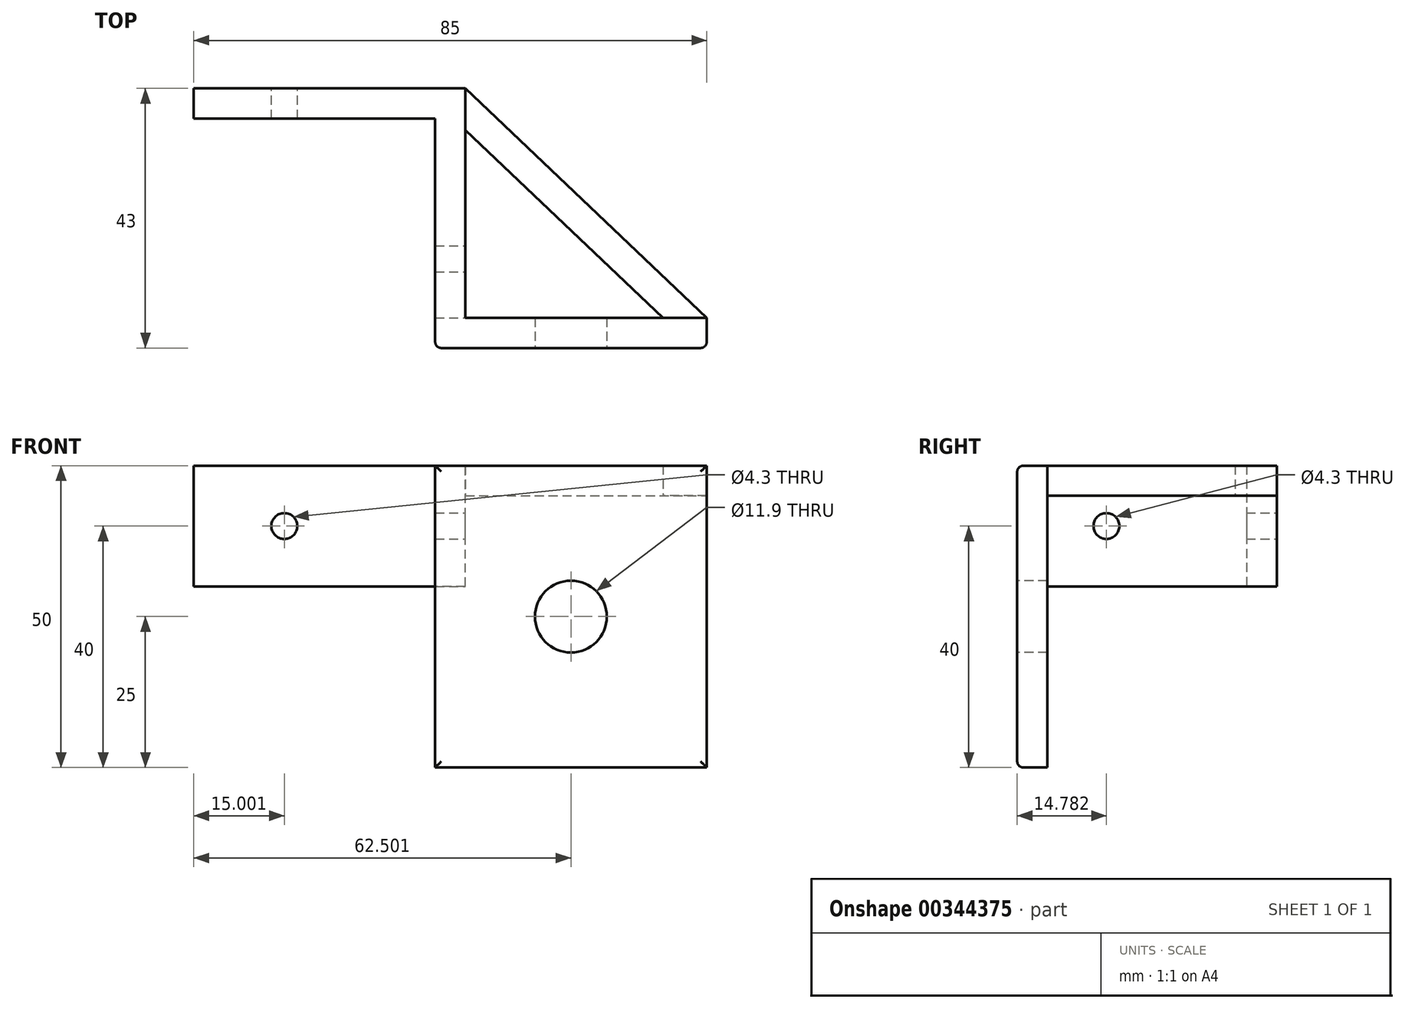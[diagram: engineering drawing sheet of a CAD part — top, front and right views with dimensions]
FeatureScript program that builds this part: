
annotation { "Feature Type Name" : "Feature", "Feature Type Description" : "" }
export const myFeature = defineFeature(function(context is Context, id is Id, definition is map)
    precondition{}
    {
        {
            assignVariable(context, id + "F0", {"name" : "panel_width", "anyValue" : 40 * mm});
        }
        {
            assignVariable(context, id + "F1", {"name" : "panel_height", "anyValue" : 50 * mm});
        }
        {
            assignVariable(context, id + "F2", {"name" : "clip_height", "anyValue" : 20 * mm});
        }
        {
            var Q0;
            Q0=qCreatedBy(makeId("Top.planeOp"),FACE);
            var sketch = newSketch(context, id + "F3", { "sketchPlane" : qUnion([Q0])});
            skLineSegment(sketch, "E0.top", {"start": v(-3.04, 17.31) * mm, "end": v(-43.04, 17.31) * mm});
            skLineSegment(sketch, "E0.left", {"start": v(-3.04, -15.69) * mm, "end": v(-3.04, 17.31) * mm});
            skPoint(sketch, "E0.middle", {"position": v(0, 0) * mm});
            skLineSegment(sketch, "E1.0", {"start": v(1.96, -20.69) * mm, "end": v(1.96, 22.31) * mm});
            skLineSegment(sketch, "E1.1", {"start": v(1.96, -20.69) * mm, "end": v(-3.04, -20.69) * mm});
            skLineSegment(sketch, "E1.3", {"start": v(1.96, 22.31) * mm, "end": v(-43.04, 22.31) * mm});
            skLineSegment(sketch, "E2", {"start": v(-43.04, 17.31) * mm, "end": v(-43.04, 22.31) * mm});
            skLineSegment(sketch, "E3", {"start": v(-3.04, -15.69) * mm, "end": v(-3.04, -20.69) * mm});
            skSolve(sketch);
        }
        {
            var Q0;
            Q0 = qSketchRegion(id + "F3", true);
            extrude(context, id + "F4", {"entities" : qUnion([Q0]), "depth" : getVariable(context, 'clip_height')});
        }
        {
            var Q0;
            Q0=makeQuery(id+"F4.opExtrude","SWEPT_FACE",FACE,{"disambiguationData":[OSD([sQuery(id+"F3.wireOp",EDGE,"E1.0")])]});
            var sketch = newSketch(context, id + "F5", { "sketchPlane" : qUnion([Q0])});
            skCircle(sketch, "E4", {"center": v(-5.9, 10) * mm, "radius": 2.15 * mm});
            skPoint(sketch, "E4.centerSnap0", {"position": v(22.31, 10) * mm});
            skLineSegment(sketch, "E5", {"start": v(-15.69, 0) * mm, "end": v(-15.69, 20) * mm});
            skSolve(sketch);
        }
        {
            var Q0;
            Q0=sQuery(id+"F5.wireOp",VERTEX,"E4.center");
            var Q1;
            Q1=makeQuery(id+"F4.opExtrude","SWEPT_BODY",BODY,{"disambiguationData":[OSD([sQuery(id+"F3.wireOp",EDGE,"E0.bottom"),sQuery(id+"F3.wireOp",EDGE,"E0.top"),sQuery(id+"F3.wireOp",EDGE,"E0.left"),sQuery(id+"F3.wireOp",EDGE,"E1.0"),sQuery(id+"F3.wireOp",EDGE,"E1.1"),sQuery(id+"F3.wireOp",EDGE,"E1.3"),sQuery(id+"F3.wireOp",EDGE,"E2"),sQuery(id+"F3.wireOp",EDGE,"msNkuylu-6MDU-LZev-BJGZ-Um7OzMUoMHMJ")])]});
            hole(context, id + "F6", {"style" : HoleStyle.SIMPLE, "endStyle" : HoleEndStyle.THROUGH, "holeDiameter" : 4.3 * mm, "isTappedThrough" : true, "tappedDepth" : 12 * mm, "tapClearance" : 3, "locations" : qUnion([Q0]), "scope" : qUnion([Q1])});
        }
        {
            var Q0;
            {var subQ0=sQuery(id+"F5.wireOp",EDGE,"E5");Q0=makeQuery(id+"F5.imprint","IMPRINT",FACE,{"disambiguationData":[TD([[makeQuery(id+"F5.imprint","IMPRINT",EDGE,{"derivedFrom":subQ0}),1.0]])]});}
            extrude(context, id + "F7", {"entities" : qUnion([Q0]), "operationType" : NewBodyOperationType.ADD, "depth" : getVariable(context, 'panel_width')});
        }
        {
            var Q0;
            {var subQ0=sQuery(id+"F3.wireOp",EDGE,"E1.0");var subQ1=makeQuery(id+"F4.opExtrude","CAP_EDGE",EDGE,{"disambiguationData":[OSD([subQ0])],"isStart":true});var subQ2=sQuery(id+"F3.wireOp",EDGE,"E1.1");Q0=makeQuery(id+"F7.boolean.opBoolean","MERGE",FACE,{"derivedFrom":[makeQuery(id+"F4.opExtrude","CAP_FACE",FACE,{"disambiguationData":[OSD([sQuery(id+"F3.wireOp",EDGE,"E0.top"),sQuery(id+"F3.wireOp",EDGE,"E0.left"),subQ0,subQ2,sQuery(id+"F3.wireOp",EDGE,"E1.3"),sQuery(id+"F3.wireOp",EDGE,"E2"),sQuery(id+"F3.wireOp",EDGE,"E3")])],"isStart":true}),makeQuery(id+"F7.opExtrude","SWEPT_FACE",FACE,{"disambiguationData":[OSD([subQ0]),TDD([makeQuery(id+"F5.imprint","IMPRINT",EDGE,{"disambiguationData":[TD([[makeQuery(id+"F5.imprint","INTERSECT",VERTEX,{"derivedFrom":[subQ1,sQuery(id+"F5.wireOp",EDGE,"E5")]}),1.0]])],"derivedFrom":subQ1})])]})]});}
            var sketch = newSketch(context, id + "F8", { "sketchPlane" : qUnion([Q0])});
            skLineSegment(sketch, "E6", {"start": v(1.96, 20.69) * mm, "end": v(1.96, 15.69) * mm});
            skSolve(sketch);
        }
        {
            var Q0;
            {var subQ0=sQuery(id+"F8.wireOp",EDGE,"E6");Q0=makeQuery(id+"F8.imprint","IMPRINT",FACE,{"disambiguationData":[TD([[makeQuery(id+"F8.imprint","IMPRINT",EDGE,{"derivedFrom":subQ0}),1.0]])]});}
            extrude(context, id + "F9", {"entities" : qUnion([Q0]), "operationType" : NewBodyOperationType.ADD, "depth" : getVariable(context, 'panel_height') - getVariable(context, 'clip_height')});
        }
        {
            var Q0;
            Q0=makeQuery(id+"F9.opExtrude","SWEPT_FACE",FACE,{"disambiguationData":[OSD([sQuery(id+"F8.wireOp",EDGE,"E6")])]});
            extrude(context, id + "F10", {"entities" : qUnion([Q0]), "operationType" : NewBodyOperationType.ADD, "depth" : 5 * mm});
        }
        {
            var Q0;
            Q0=makeQuery(id+"F4.opExtrude","SWEPT_FACE",FACE,{"disambiguationData":[OSD([sQuery(id+"F3.wireOp",EDGE,"E1.3")])]});
            var sketch = newSketch(context, id + "F11", { "sketchPlane" : qUnion([Q0])});
            skPoint(sketch, "E7.centerSnap0", {"position": v(-1.96, 10) * mm});
            skPoint(sketch, "E7.centerSnap1", {"position": v(20.54, 20) * mm});
            skCircle(sketch, "E8", {"center": v(28.04, 10) * mm, "radius": 2.15 * mm});
            skSolve(sketch);
        }
        {
            var Q0;
            Q0=sQuery(id+"F11.wireOp",VERTEX,"E8.center");
            var Q1;
            Q1=makeQuery(id+"F4.opExtrude","SWEPT_BODY",BODY,{"disambiguationData":[OSD([sQuery(id+"F3.wireOp",EDGE,"E0.bottom"),sQuery(id+"F3.wireOp",EDGE,"E0.top"),sQuery(id+"F3.wireOp",EDGE,"E0.left"),sQuery(id+"F3.wireOp",EDGE,"E1.0"),sQuery(id+"F3.wireOp",EDGE,"E1.1"),sQuery(id+"F3.wireOp",EDGE,"E1.3"),sQuery(id+"F3.wireOp",EDGE,"E2"),sQuery(id+"F3.wireOp",EDGE,"msNkuylu-6MDU-LZev-BJGZ-Um7OzMUoMHMJ")])]});
            hole(context, id + "F12", {"style" : HoleStyle.SIMPLE, "endStyle" : HoleEndStyle.BLIND, "holeDiameter" : 4.3 * mm, "holeDepth" : 5 * mm, "isTappedThrough" : true, "tappedDepth" : 12 * mm, "tapClearance" : 3, "locations" : qUnion([Q0]), "scope" : qUnion([Q1])});
        }
        {
            var Q0;
            {var subQ0=sQuery(id+"F3.wireOp",EDGE,"E1.1");var subQ1=sQuery(id+"F3.wireOp",EDGE,"E1.0");Q0=makeQuery(id+"F10.boolean.opBoolean","MERGE",FACE,{"derivedFrom":[makeQuery(id+"F9.boolean.opBoolean","MERGE",FACE,{"derivedFrom":[makeQuery(id+"F7.boolean.opBoolean","MERGE",FACE,{"derivedFrom":[makeQuery(id+"F4.opExtrude","SWEPT_FACE",FACE,{"disambiguationData":[OSD([subQ0])]}),makeQuery(id+"F7.opExtrude","SWEPT_FACE",FACE,{"disambiguationData":[OSD([subQ1,subQ0])]})]}),makeQuery(id+"F9.opExtrude","SWEPT_FACE",FACE,{"disambiguationData":[OSD([subQ1,subQ0])]})]}),makeQuery(id+"F10.opExtrude","SWEPT_FACE",FACE,{"disambiguationData":[OSD([subQ1,subQ0,sQuery(id+"F8.wireOp",EDGE,"E6")])]})]});}
            var sketch = newSketch(context, id + "F13", { "sketchPlane" : qUnion([Q0])});
            skCircle(sketch, "E9", {"center": v(19.46, -5) * mm, "radius": 5.95 * mm});
            skSolve(sketch);
        }
        {
            var Q0;
            Q0=makeQuery(id+"F13.imprint","IMPRINT",FACE,{"disambiguationData":[TD([[makeQuery(id+"F13.imprint","IMPRINT",EDGE,{"derivedFrom":sQuery(id+"F13.wireOp",EDGE,"E9")}),1.0]])]});
            var Q1;
            {var subQ0=sQuery(id+"F5.wireOp",EDGE,"E5");var subQ1=sQuery(id+"F3.wireOp",EDGE,"E1.0");Q1=makeQuery(id+"F10.boolean.opBoolean","MERGE",FACE,{"derivedFrom":[makeQuery(id+"F9.boolean.opBoolean","MERGE",FACE,{"derivedFrom":[makeQuery(id+"F7.opExtrude","SWEPT_FACE",FACE,{"disambiguationData":[OSD([subQ0])]}),makeQuery(id+"F9.opExtrude","SWEPT_FACE",FACE,{"disambiguationData":[OSD([subQ1,subQ0])]})]}),makeQuery(id+"F10.opExtrude","SWEPT_FACE",FACE,{"disambiguationData":[OSD([subQ1,subQ0,sQuery(id+"F8.wireOp",EDGE,"E6")])]})]});}
            extrude(context, id + "F14", {"entities" : qUnion([Q0]), "operationType" : NewBodyOperationType.REMOVE, "endBound" : BoundingType.UP_TO_SURFACE, "oppositeDirection" : true, "endBoundEntityFace" : qUnion([Q1]), "depth" : 4.25 * mm});
        }
        {
            var Q0;
            Q0=qCreatedBy(makeId("Top.planeOp"),FACE);
            var sketch = newSketch(context, id + "F15", { "sketchPlane" : qUnion([Q0])});
            skLineSegment(sketch, "E10.0", {"start": v(1.96, 15.41) * mm, "end": v(1.96, 22.31) * mm});
            skLineSegment(sketch, "E11.0", {"start": v(41.96, -15.69) * mm, "end": v(34.7, -15.69) * mm});
            skLineSegment(sketch, "E12", {"start": v(1.96, 22.31) * mm, "end": v(41.96, -15.69) * mm});
            skLineSegment(sketch, "E13", {"start": v(1.96, 15.41) * mm, "end": v(34.7, -15.69) * mm});
            skPoint(sketch, "E14.orphan", {"position": v(1.96, -15.69) * mm});
            skPoint(sketch, "E15.0", {"position": v(41.96, -15.69) * mm});
            skSolve(sketch);
        }
        {
            var Q0;
            Q0=makeQuery(id+"F15.imprint","IMPRINT",FACE,{"disambiguationData":[TD([[makeQuery(id+"F15.imprint","IMPRINT",EDGE,{"derivedFrom":sQuery(id+"F15.wireOp",EDGE,"E10.0")}),-1.0]])]});
            extrude(context, id + "F16", {"entities" : qUnion([Q0]), "depth" : 5 * mm});
        }
        {
            var Q0;
            Q0=makeQuery(id+"F16.opExtrude","SWEPT_BODY",BODY,{"disambiguationData":[OSD([sQuery(id+"F15.wireOp",EDGE,"E10.0"),sQuery(id+"F15.wireOp",EDGE,"E11.0"),sQuery(id+"F15.wireOp",EDGE,"E12"),sQuery(id+"F15.wireOp",EDGE,"E13")])]});
            transform(context, id + "F17", {"entities" : qUnion([Q0]), "transformType" : TransformType.TRANSLATION_3D, "dx" : 0 * mm, "dy" : 0 * mm, "dz" : getVariable(context, 'clip_height') - 5 * mm, "makeCopy" : false});
        }
        {
            var Q0;
            Q0=makeQuery(id+"F9.opExtrude","CAP_EDGE",EDGE,{"disambiguationData":[OSD([sQuery(id+"F3.wireOp",EDGE,"E1.0"),sQuery(id+"F3.wireOp",EDGE,"E1.1")])],"isStart":false});
            var Q1;
            Q1=makeQuery(id+"F4.opExtrude","SWEPT_EDGE",EDGE,{"disambiguationData":[OSD([sQuery(id+"F3.wireOp",EDGE,"E1.1"),sQuery(id+"F3.wireOp",EDGE,"msNkuylu-6MDU-LZev-BJGZ-Um7OzMUoMHMJ")])]});
            var Q2;
            Q2=makeQuery(id+"F10.opExtrude","CAP_EDGE",EDGE,{"disambiguationData":[OSD([sQuery(id+"F3.wireOp",EDGE,"E1.0"),sQuery(id+"F3.wireOp",EDGE,"E1.1"),sQuery(id+"F8.wireOp",EDGE,"E6")])],"isStart":false});
            var Q3;
            {var subQ0=sQuery(id+"F3.wireOp",EDGE,"E1.1");var subQ1=sQuery(id+"F3.wireOp",EDGE,"E1.0");Q3=makeQuery(id+"F9.boolean.opBoolean","MERGE",EDGE,{"derivedFrom":[makeQuery(id+"F7.opExtrude","CAP_EDGE",EDGE,{"disambiguationData":[OSD([subQ1,subQ0])],"isStart":false}),makeQuery(id+"F9.opExtrude","SWEPT_EDGE",EDGE,{"disambiguationData":[OSD([subQ1,subQ0])]})]});}
            var Q4;
            {var subQ0=sQuery(id+"F3.wireOp",EDGE,"E1.0");var subQ1=sQuery(id+"F3.wireOp",EDGE,"E1.1");Q4=makeQuery(id+"F7.boolean.opBoolean","MERGE",EDGE,{"derivedFrom":[makeQuery(id+"F4.opExtrude","CAP_EDGE",EDGE,{"disambiguationData":[OSD([subQ1])],"isStart":false}),makeQuery(id+"F7.opExtrude","SWEPT_EDGE",EDGE,{"disambiguationData":[OSD([subQ0,subQ1]),TDD([makeQuery(id+"F5.imprint","INTERSECT",VERTEX,{"derivedFrom":[makeQuery(id+"F4.opExtrude","SWEPT_EDGE",EDGE,{"disambiguationData":[OSD([subQ0,subQ1])]}),makeQuery(id+"F4.opExtrude","CAP_EDGE",EDGE,{"disambiguationData":[OSD([subQ0])],"isStart":false})]})])]})]});}
            fillet(context, id + "F18", {"entities" : qUnion([Q0, Q1, Q2, Q3, Q4]), "radius" : 1 * mm, "tangentPropagation" : true, "allowEdgeOverflow" : false});
        }
    });
